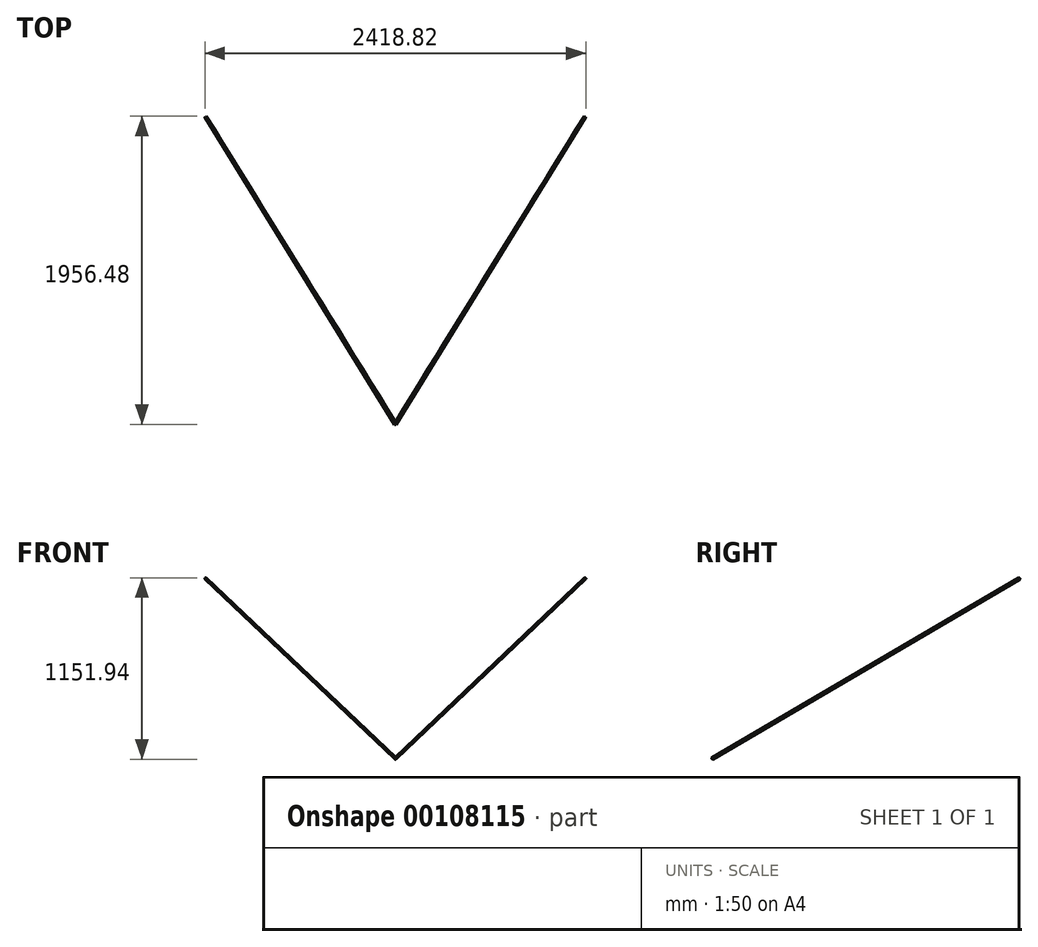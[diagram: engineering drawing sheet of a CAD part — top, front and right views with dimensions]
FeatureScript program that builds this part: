
annotation { "Feature Type Name" : "Feature", "Feature Type Description" : "" }
export const myFeature = defineFeature(function(context is Context, id is Id, definition is map)
    precondition{}
    {
        {
            assignVariable(context, id + "F0", {"name" : "Y1", "anyValue" : 0});
        }
        {
            var Q0;
            Q0=qCreatedBy(makeId("Front.planeOp"),FACE);
            cPlane(context, id + "F1", {"entities" : qUnion([Q0]), "cplaneType" : CPlaneType.OFFSET, "offset" : (getVariable(context, 'Y1')) * mm, "width" : 150 * mm, "height" : 150 * mm});
        }
        {
            var Q0;
            Q0=qCreatedBy(id+"F1.planeOp",FACE);
            var sketch = newSketch(context, id + "F2", { "sketchPlane" : qUnion([Q0])});
            skPoint(sketch, "E0", {"position": v(-1205, 5800) * mm});
            skPoint(sketch, "E1", {"position": v(-1205, 0) * mm});
            skSolve(sketch);
        }
        {
            assignVariable(context, id + "F3", {"name" : "Y2", "anyValue" : 3900 / 2});
        }
        {
            var Q0;
            Q0=qCreatedBy(makeId("Front.planeOp"),FACE);
            cPlane(context, id + "F4", {"entities" : qUnion([Q0]), "cplaneType" : CPlaneType.OFFSET, "offset" : (getVariable(context, 'Y2')) * mm, "width" : 150 * mm, "height" : 150 * mm});
        }
        {
            var Q0;
            Q0=qCreatedBy(id+"F4.planeOp",FACE);
            var sketch = newSketch(context, id + "F5", { "sketchPlane" : qUnion([Q0])});
            skPoint(sketch, "E2", {"position": v(0, 4657) * mm});
            skSolve(sketch);
        }
        {
            var Q0;
            Q0=sQuery(id+"F2.wireOp",VERTEX,"E0");
            var Q1;
            Q1=sQuery(id+"F2.wireOp",VERTEX,"E1");
            var Q2;
            Q2=sQuery(id+"F5.wireOp",VERTEX,"E2");
            cPlane(context, id + "F6", {"entities" : qUnion([Q0, Q1, Q2]), "cplaneType" : CPlaneType.THREE_POINT, "offset" : 25 * mm, "width" : 150 * mm, "height" : 150 * mm});
        }
        {
            var Q0;
            Q0=qCreatedBy(id+"F6.planeOp",FACE);
            var sketch = newSketch(context, id + "F7", { "sketchPlane" : qUnion([Q0])});
            skPoint(sketch, "E3.0", {"position": v(633.44, 5800) * mm});
            skPoint(sketch, "E4.0", {"position": v(-1658.83, 4657) * mm});
            skLineSegment(sketch, "E5", {"start": v(633.44, 5800) * mm, "end": v(-1658.83, 4657) * mm});
            skSolve(sketch);
        }
        {
            var Q0;
            Q0=sQuery(id+"F7.wireOp",VERTEX,"E3.0");
            var Q1;
            Q1=sQuery(id+"F7.wireOp",EDGE,"E5");
            cPlane(context, id + "F8", {"entities" : qUnion([Q0, Q1]), "cplaneType" : CPlaneType.LINE_POINT, "offset" : 25 * mm, "width" : 150 * mm, "height" : 150 * mm});
        }
        {
            var Q0;
            Q0=qCreatedBy(id+"F8.planeOp",FACE);
            var sketch = newSketch(context, id + "F9", { "sketchPlane" : qUnion([Q0])});
            skPoint(sketch, "E6.0", {"position": v(316.45, 5003.76) * mm});
            skCircle(sketch, "E7", {"center": v(316.45, 5003.76) * mm, "radius": 5 * mm});
            skSolve(sketch);
        }
        {
            var Q0;
            Q0=makeQuery(id+"F9.imprint","IMPRINT",FACE,{"disambiguationData":[TD([[makeQuery(id+"F9.imprint","IMPRINT",EDGE,{"derivedFrom":sQuery(id+"F9.wireOp",EDGE,"E7")}),1.0]])]});
            var Q1;
            Q1=sQuery(id+"F7.wireOp",EDGE,"E5");
            sweep(context, id + "F10", {"profiles" : qUnion([Q0]), "path" : qUnion([Q1])});
        }
        {
            var Q0;
            Q0=makeQuery(id+"F10.opSweep","SWEPT_BODY",BODY,{"disambiguationData":[OSD([sQuery(id+"F7.wireOp",EDGE,"E5"),sQuery(id+"F9.wireOp",EDGE,"E7")])]});
            var Q1;
            Q1=qCreatedBy(makeId("Right.planeOp"),FACE);
            mirror(context, id + "F11", {"operationType" : NewBodyOperationType.ADD, "entities" : qUnion([Q0]), "mirrorPlane" : qUnion([Q1])});
        }
    });
